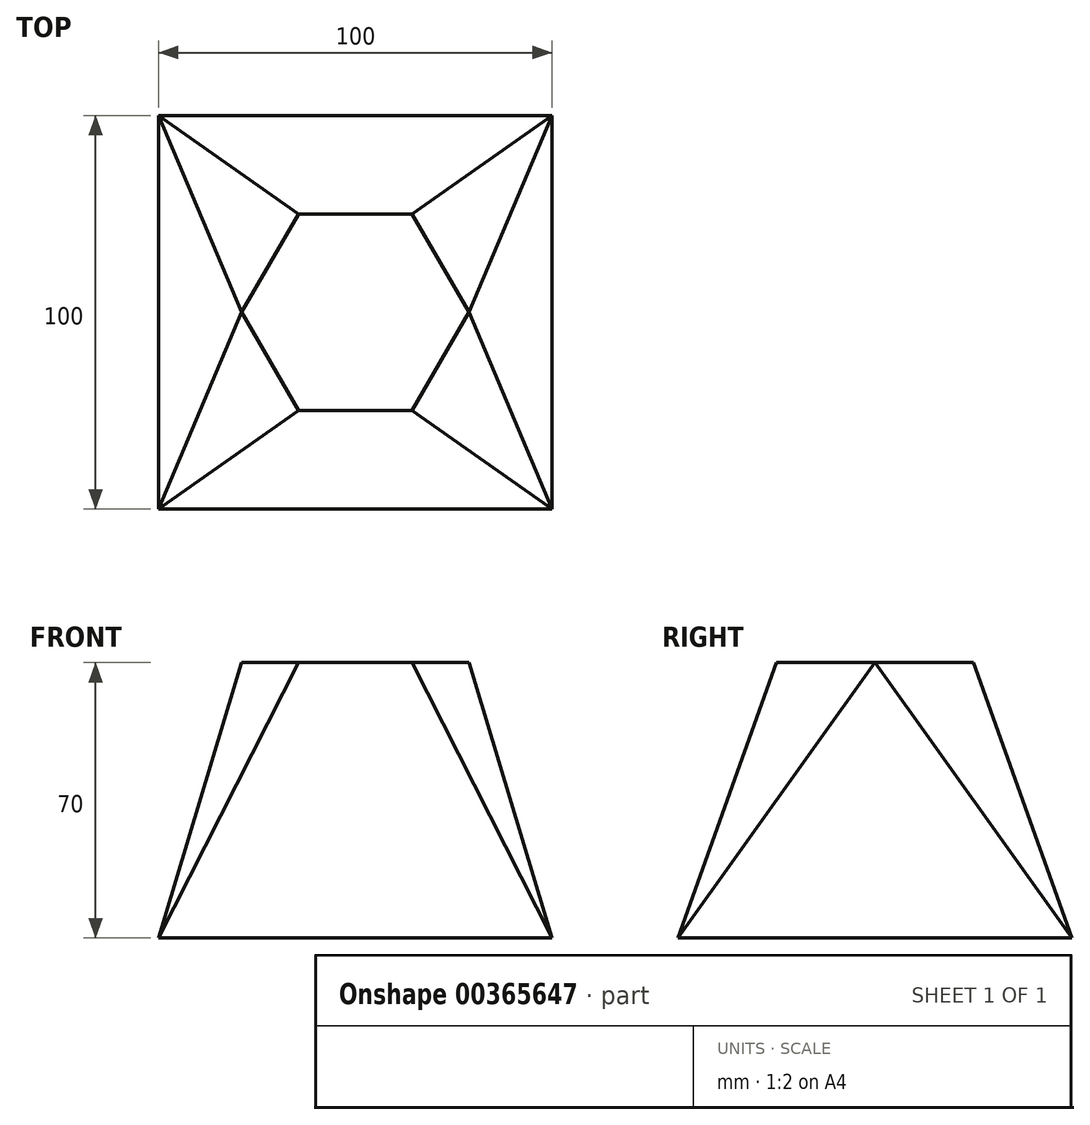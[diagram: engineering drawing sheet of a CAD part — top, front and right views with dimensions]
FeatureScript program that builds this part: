
annotation { "Feature Type Name" : "Feature", "Feature Type Description" : "" }
export const myFeature = defineFeature(function(context is Context, id is Id, definition is map)
    precondition{}
    {
        {
            var Q0;
            Q0=qCreatedBy(makeId("Top.planeOp"),FACE);
            var sketch = newSketch(context, id + "F0", { "sketchPlane" : qUnion([Q0])});
            skLineSegment(sketch, "E0.bottom", {"start": v(50, 50) * mm, "end": v(-50, 50) * mm});
            skLineSegment(sketch, "E0.top", {"start": v(50, -50) * mm, "end": v(-50, -50) * mm});
            skLineSegment(sketch, "E0.left", {"start": v(50, 50) * mm, "end": v(50, -50) * mm});
            skLineSegment(sketch, "E0.right", {"start": v(-50, 50) * mm, "end": v(-50, -50) * mm});
            skPoint(sketch, "E0.middle", {"position": v(0, 0) * mm});
            skSolve(sketch);
        }
        {
            var Q0;
            Q0=qCreatedBy(makeId("Top.planeOp"),FACE);
            cPlane(context, id + "F1", {"entities" : qUnion([Q0]), "cplaneType" : CPlaneType.OFFSET, "offset" : 70 * mm, "width" : 150 * mm, "height" : 150 * mm});
        }
        {
            var Q0;
            Q0=qCreatedBy(id+"F1.planeOp",FACE);
            var sketch = newSketch(context, id + "F2", { "sketchPlane" : qUnion([Q0])});
            skCircle(sketch, "E1.cCircle", {"center": v(0, 0) * mm, "radius": 25 * mm, "construction": true});
            skLineSegment(sketch, "E1.0", {"start": v(-14.43, 25) * mm, "end": v(14.43, 25) * mm});
            skLineSegment(sketch, "E1.1", {"start": v(14.43, 25) * mm, "end": v(28.87, 0) * mm});
            skLineSegment(sketch, "E1.2", {"start": v(28.87, 0) * mm, "end": v(14.43, -25) * mm});
            skLineSegment(sketch, "E1.3", {"start": v(14.43, -25) * mm, "end": v(-14.43, -25) * mm});
            skLineSegment(sketch, "E1.4", {"start": v(-14.43, -25) * mm, "end": v(-28.87, 0) * mm});
            skLineSegment(sketch, "E1.5", {"start": v(-28.87, 0) * mm, "end": v(-14.43, 25) * mm});
            skPoint(sketch, "E1.0.midPoint", {"position": v(0, 25) * mm});
            skLineSegment(sketch, "E2", {"start": v(-14.43, 25) * mm, "end": v(-14.43, -25) * mm});
            skLineSegment(sketch, "E3", {"start": v(14.43, 25) * mm, "end": v(14.43, -25) * mm});
            skSolve(sketch);
        }
        {
            var Q0;
            Q0=makeQuery(id+"F2.imprint","IMPRINT",FACE,{"disambiguationData":[TD([[makeQuery(id+"F2.imprint","IMPRINT",EDGE,{"derivedFrom":sQuery(id+"F2.wireOp",EDGE,"E1.0")}),-1.0]])]});
            var Q1;
            Q1=makeQuery(id+"F0.imprint","IMPRINT",FACE,{"disambiguationData":[TD([[makeQuery(id+"F0.imprint","IMPRINT",EDGE,{"derivedFrom":sQuery(id+"F0.wireOp",EDGE,"E0.bottom")}),1.0]])]});
            loft(context, id + "F3", {"sheetProfilesArray" : [{ "sheetProfileEntities" : qUnion([Q0]) }, { "sheetProfileEntities" : qUnion([Q1]) }]});
        }
        {
            var Q1;
            Q1=makeQuery(id+"F2.imprint","IMPRINT",FACE,{"disambiguationData":[TD([[makeQuery(id+"F2.imprint","IMPRINT",EDGE,{"derivedFrom":sQuery(id+"F2.wireOp",EDGE,"E1.4")}),-1.0]])]});
            var Q2;
            Q2=makeQuery(id+"F3.opLoft","MID_CAP_VERTEX",VERTEX,{"disambiguationData":[OSD([sQuery(id+"F0.wireOp",EDGE,"E0.top"),sQuery(id+"F0.wireOp",EDGE,"E0.right")])],"capPos":1.0});
            loft(context, id + "F4", {"operationType" : NewBodyOperationType.ADD, "sheetProfilesArray" : [{ "sheetProfileEntities" : qUnion([Q1]) }, { "sheetProfileEntities" : qUnion([Q2]) }]});
        }
        {
            var Q1;
            Q1=makeQuery(id+"F2.imprint","IMPRINT",FACE,{"disambiguationData":[TD([[makeQuery(id+"F2.imprint","IMPRINT",EDGE,{"derivedFrom":sQuery(id+"F2.wireOp",EDGE,"E1.4")}),-1.0]])]});
            var Q2;
            Q2=makeQuery(id+"F3.opLoft","MID_CAP_VERTEX",VERTEX,{"disambiguationData":[OSD([sQuery(id+"F0.wireOp",EDGE,"E0.bottom"),sQuery(id+"F0.wireOp",EDGE,"E0.right")])],"capPos":1.0});
            loft(context, id + "F5", {"operationType" : NewBodyOperationType.ADD, "sheetProfilesArray" : [{ "sheetProfileEntities" : qUnion([Q1]) }, { "sheetProfileEntities" : qUnion([Q2]) }]});
        }
        {
            var Q1;
            Q1=makeQuery(id+"F5.opLoft","SWEPT_FACE",FACE,{"disambiguationData":[OSD([sQuery(id+"F2.wireOp",EDGE,"E1.3"),sQuery(id+"F2.wireOp",EDGE,"E1.4"),sQuery(id+"F2.wireOp",EDGE,"E1.5"),sQuery(id+"F2.wireOp",EDGE,"E2")])]});
            var Q2;
            Q2=makeQuery(id+"F4.opLoft","SWEPT_FACE",FACE,{"disambiguationData":[OSD([sQuery(id+"F2.wireOp",EDGE,"E1.0"),sQuery(id+"F2.wireOp",EDGE,"E1.4"),sQuery(id+"F2.wireOp",EDGE,"E1.5"),sQuery(id+"F2.wireOp",EDGE,"E2")])]});
            var Q3;
            Q3=makeQuery(id+"F3.opLoft","MID_CAP_EDGE",EDGE,{"disambiguationData":[OSD([sQuery(id+"F0.wireOp",EDGE,"E0.bottom"),sQuery(id+"F0.wireOp",EDGE,"E0.top"),sQuery(id+"F0.wireOp",EDGE,"E0.right")])],"capPos":1.0});
            loft(context, id + "F6", {"operationType" : NewBodyOperationType.ADD, "addGuides" : true, "sheetProfilesArray" : [{ "sheetProfileEntities" : qUnion([Q1]) }, { "sheetProfileEntities" : qUnion([Q2]) }], "guidesArray" : [{ "guideEntities" : qUnion([Q3]), "guideDerivativeType" : LoftGuideDerivativeType.DEFAULT, "guideDerivativeMagnitude" : 1 }]});
        }
        {
            var Q1;
            Q1=makeQuery(id+"F2.imprint","IMPRINT",FACE,{"disambiguationData":[TD([[makeQuery(id+"F2.imprint","IMPRINT",EDGE,{"derivedFrom":sQuery(id+"F2.wireOp",EDGE,"E1.1")}),-1.0]])]});
            var Q2;
            Q2=makeQuery(id+"F3.opLoft","MID_CAP_VERTEX",VERTEX,{"disambiguationData":[OSD([sQuery(id+"F0.wireOp",EDGE,"E0.top"),sQuery(id+"F0.wireOp",EDGE,"E0.left")])],"capPos":1.0});
            loft(context, id + "F7", {"operationType" : NewBodyOperationType.ADD, "sheetProfilesArray" : [{ "sheetProfileEntities" : qUnion([Q1]) }, { "sheetProfileEntities" : qUnion([Q2]) }]});
        }
        {
            var Q1;
            Q1=makeQuery(id+"F2.imprint","IMPRINT",FACE,{"disambiguationData":[TD([[makeQuery(id+"F2.imprint","IMPRINT",EDGE,{"derivedFrom":sQuery(id+"F2.wireOp",EDGE,"E1.1")}),-1.0]])]});
            var Q2;
            Q2=makeQuery(id+"F3.opLoft","MID_CAP_VERTEX",VERTEX,{"disambiguationData":[OSD([sQuery(id+"F0.wireOp",EDGE,"E0.bottom"),sQuery(id+"F0.wireOp",EDGE,"E0.left")])],"capPos":1.0});
            loft(context, id + "F8", {"operationType" : NewBodyOperationType.ADD, "sheetProfilesArray" : [{ "sheetProfileEntities" : qUnion([Q1]) }, { "sheetProfileEntities" : qUnion([Q2]) }]});
        }
        {
            var Q1;
            Q1=makeQuery(id+"F8.opLoft","SWEPT_FACE",FACE,{"disambiguationData":[OSD([sQuery(id+"F2.wireOp",EDGE,"E1.1"),sQuery(id+"F2.wireOp",EDGE,"E1.2"),sQuery(id+"F2.wireOp",EDGE,"E1.3"),sQuery(id+"F2.wireOp",EDGE,"E3")])]});
            var Q2;
            Q2=makeQuery(id+"F7.opLoft","SWEPT_FACE",FACE,{"disambiguationData":[OSD([sQuery(id+"F2.wireOp",EDGE,"E1.0"),sQuery(id+"F2.wireOp",EDGE,"E1.1"),sQuery(id+"F2.wireOp",EDGE,"E1.2"),sQuery(id+"F2.wireOp",EDGE,"E3")])]});
            var Q3;
            Q3=makeQuery(id+"F3.opLoft","MID_CAP_EDGE",EDGE,{"disambiguationData":[OSD([sQuery(id+"F0.wireOp",EDGE,"E0.bottom"),sQuery(id+"F0.wireOp",EDGE,"E0.top"),sQuery(id+"F0.wireOp",EDGE,"E0.left")])],"capPos":1.0});
            loft(context, id + "F9", {"operationType" : NewBodyOperationType.ADD, "addGuides" : true, "sheetProfilesArray" : [{ "sheetProfileEntities" : qUnion([Q1]) }, { "sheetProfileEntities" : qUnion([Q2]) }], "guidesArray" : [{ "guideEntities" : qUnion([Q3]), "guideDerivativeType" : LoftGuideDerivativeType.DEFAULT, "guideDerivativeMagnitude" : 1 }]});
        }
    });
